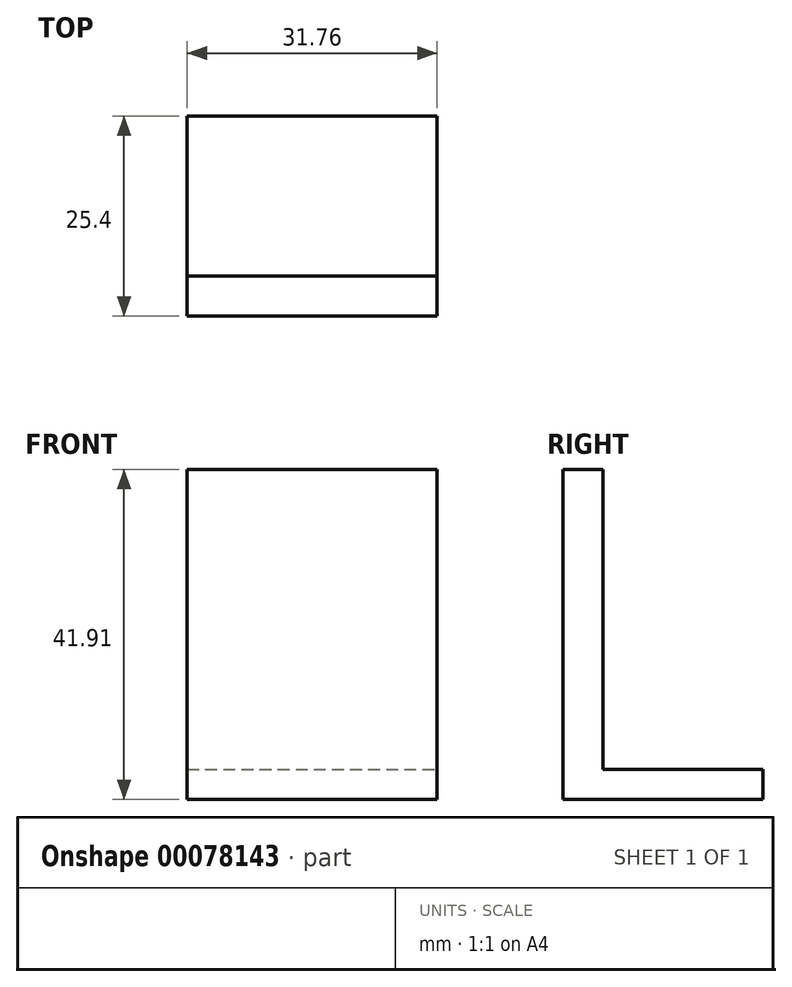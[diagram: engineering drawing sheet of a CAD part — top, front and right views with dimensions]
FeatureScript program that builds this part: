
annotation { "Feature Type Name" : "Feature", "Feature Type Description" : "" }
export const myFeature = defineFeature(function(context is Context, id is Id, definition is map)
    precondition{}
    {
        {
            var Q0;
            Q0=qCreatedBy(makeId("Top.planeOp"),FACE);
            var sketch = newSketch(context, id + "F0", { "sketchPlane" : qUnion([Q0])});
            skLineSegment(sketch, "E0.bottom", {"start": v(-15.88, 12.7) * mm, "end": v(15.88, 12.7) * mm});
            skLineSegment(sketch, "E0.top", {"start": v(-15.87, -12.7) * mm, "end": v(15.87, -12.7) * mm});
            skLineSegment(sketch, "E0.left", {"start": v(-15.88, 12.7) * mm, "end": v(-15.88, -12.7) * mm});
            skLineSegment(sketch, "E0.right", {"start": v(15.88, 12.7) * mm, "end": v(15.87, -12.7) * mm});
            skPoint(sketch, "E0.middle", {"position": v(0, 0) * mm});
            skLineSegment(sketch, "E1", {"start": v(-15.87, -6.35) * mm, "end": v(15.88, -6.35) * mm});
            skSolve(sketch);
        }
        {
            var Q0;
            {var subQ0=sQuery(id+"F0.wireOp",EDGE,"E0.bottom");Q0=makeQuery(id+"F0.imprint","IMPRINT",FACE,{"disambiguationData":[TD([[makeQuery(id+"F0.imprint","IMPRINT",EDGE,{"derivedFrom":subQ0}),-1.0]])]});}
            var Q1;
            {var subQ0=sQuery(id+"F0.wireOp",EDGE,"E0.top");Q1=makeQuery(id+"F0.imprint","IMPRINT",FACE,{"disambiguationData":[TD([[makeQuery(id+"F0.imprint","IMPRINT",EDGE,{"derivedFrom":subQ0}),1.0]])]});}
            extrude(context, id + "F1", {"entities" : qUnion([Q0, Q1]), "depth" : 3.8 * mm});
        }
        {
            var Q0;
            Q0=makeQuery(id+"F1.opExtrude","CAP_FACE",FACE,{"disambiguationData":[OSD([sQuery(id+"F0.wireOp",EDGE,"E0.bottom"),sQuery(id+"F0.wireOp",EDGE,"E0.top"),sQuery(id+"F0.wireOp",EDGE,"E0.left"),sQuery(id+"F0.wireOp",EDGE,"E0.right")])],"isStart":false});
            var sketch = newSketch(context, id + "F2", { "sketchPlane" : qUnion([Q0])});
            skLineSegment(sketch, "E2", {"start": v(-15.88, -7.62) * mm, "end": v(15.88, -7.62) * mm});
            skSolve(sketch);
        }
        {
            var Q0;
            {var subQ0=sQuery(id+"F2.wireOp",EDGE,"E2");Q0=makeQuery(id+"F2.imprint","IMPRINT",FACE,{"disambiguationData":[TD([[makeQuery(id+"F2.imprint","IMPRINT",EDGE,{"derivedFrom":subQ0}),-1.0]])]});}
            extrude(context, id + "F3", {"entities" : qUnion([Q0]), "operationType" : NewBodyOperationType.ADD, "depth" : 38.1 * mm});
        }
    });
